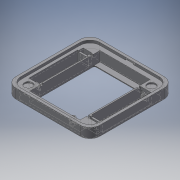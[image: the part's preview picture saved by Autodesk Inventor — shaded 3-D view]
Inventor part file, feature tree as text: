
AUTODESK INVENTOR PART (.ipt)
format: ipt  version: 2016 SP2 (Build 200236200, 236)  size: 422,912 bytes
history: native  units: mm
features: extrude x11, sketch x11, fillet x1, chamfer x1
ambient origin geometry x8: Origin, YZ Plane, XZ Plane, XY Plane, X Axis, Y Axis, Z Axis, Center Point
bodies: Volumenkörper1 (feature_tree)
feature tree (24):
  extrude  "Extrusion1"  Depth=70.3mm
  extrude  "Extrusion2"  Depth=5.0mm
  extrude  "Extrusion7"  Depth=10.5mm
  extrude  "Extrusion8"  Depth=48.8mm
  extrude  "Extrusion9"  Depth=1.2mm
  extrude  "Extrusion10"  Depth=0.8mm
  extrude  "Extrusion12"  Depth=3.0mm
  extrude  "Extrusion13"  Depth=2.0mm
  extrude  "Extrusion14"  Depth=0.5mm
  extrude  "Extrusion15"  Depth=0.8mm
  fillet  "Rundung1"  Radius=0.5mm
  chamfer  "Fase3"  Distance=3.75mm
  extrude  "Extrusion17"  Depth=2.0mm
  sketch  "Skizze1"  dims[d0=50.3mm d1=70.3mm]
  sketch  "Skizze2"  dims[d2=5.0mm d3=5.0mm]
  sketch  "Skizze7"  dims[d4=10.5mm d5=10.5mm]
  sketch  "Skizze8"  dims[d6=48.8mm d7=48.8mm]
  sketch  "Skizze9"  dims[d8=1.2mm d9=1.2mm]
  sketch  "Skizze10"  dims[d11=0.8mm d12=0.8mm]
  sketch  "Skizze12"  dims[d13=0.8mm d14=3.0mm]
  sketch  "Skizze13"  dims[d15=3.75mm d16=2.0mm]
  sketch  "Skizze14"  dims[d17=3.0mm d18=0.5mm]
  sketch  "Skizze15"  dims[d19=0.5mm d20=0.8mm d21=0.5mm d22=0.5mm]
  sketch  "Skizze17"  dims[d23=3.0mm d26=3.75mm d27=2.0mm d28=0.5mm d30=3.0mm d31=0.8mm d32=0.8mm d33=1.6mm d34=1.0mm d35=1.0mm d36=3.0mm d37=3.0mm d38=1.0mm d39=1.0mm d40=1.6mm d41=10.0mm d42=0.0mm d43=5.6mm d44=59.0mm d45=2.0mm d46=0.8mm d47=0.0mm d80=8.15mm d81=8.15mm d82=6.0mm d83=6.0mm d84=6.0mm d85=6.0mm d86=1.4mm d87=0.0mm d88=3.0mm d89=3.0mm d90=3.8mm d91=0.0mm d92=3.0mm d93=3.0mm d94=3.8mm d95=0.0mm d96=8.5mm d97=0.5mm d98=0.5mm d99=2.0mm d100=0.5mm d101=2.0mm d102=0.5mm d103=1.6mm d104=8.5mm d105=2.0mm d106=0.5mm d107=1.5mm d108=0.0mm d122=2.6mm d123=0.0mm d124=1.9mm d125=0.6mm d126=5.2mm d127=1.0mm d128=5.2mm d129=1.0mm d130=1.2mm d131=0.0mm d132=4.1mm d133=1.0mm d134=8.2mm d135=1.2mm d136=0.0mm d137=10.8mm d138=0.0mm d139=10.0mm d140=5.3mm d141=1.2mm d142=6.108652mm d147=1.35mm d148=1.35mm d149=3.0mm d150=2.85mm d151=5.0mm d152=5.0mm d153=5.0mm d154=2.85mm d155=10.15mm d156=10.15mm d157=2.85mm d158=10.15mm d159=10.15mm d160=2.85mm d161=3.0mm d162=5.0mm d163=3.0mm d164=3.0mm d165=6.0mm d166=0.0mm]
